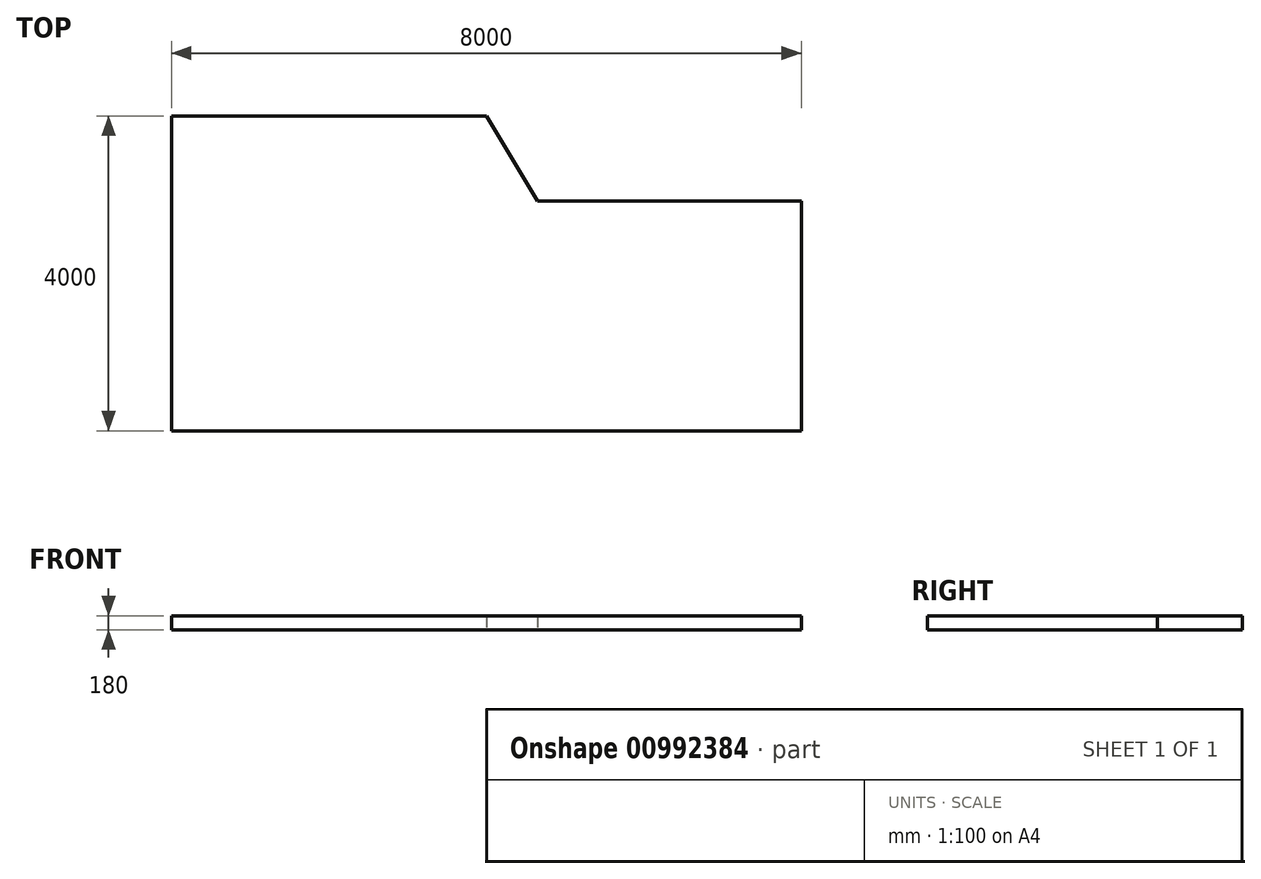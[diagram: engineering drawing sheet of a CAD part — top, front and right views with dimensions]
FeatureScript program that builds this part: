
annotation { "Feature Type Name" : "Feature", "Feature Type Description" : "" }
export const myFeature = defineFeature(function(context is Context, id is Id, definition is map)
    precondition{}
    {
        {
            var Q0;
            Q0=qCreatedBy(makeId("Top.planeOp"),FACE);
            var sketch = newSketch(context, id + "F0", { "sketchPlane" : qUnion([Q0])});
            skLineSegment(sketch, "E0", {"start": v(0, 630.05) * mm, "end": v(0, 4630.05) * mm});
            skLineSegment(sketch, "E1", {"start": v(4000, 4630.05) * mm, "end": v(0, 4630.05) * mm});
            skLineSegment(sketch, "E2", {"start": v(4000, 4630.05) * mm, "end": v(4650.71, 3551.62) * mm});
            skLineSegment(sketch, "E3", {"start": v(4650.71, 3551.62) * mm, "end": v(8000, 3551.62) * mm});
            skLineSegment(sketch, "E4", {"start": v(0, 630.05) * mm, "end": v(8000, 630.05) * mm});
            skLineSegment(sketch, "E5", {"start": v(8000, 3551.62) * mm, "end": v(8000, 630.05) * mm});
            skSolve(sketch);
        }
        {
            var Q0;
            Q0 = qSketchRegion(id + "F0", true);
            extrude(context, id + "F1", {"entities" : qUnion([Q0]), "depth" : 180 * mm, "offsetDistance" : 25.4 * mm});
        }
    });
